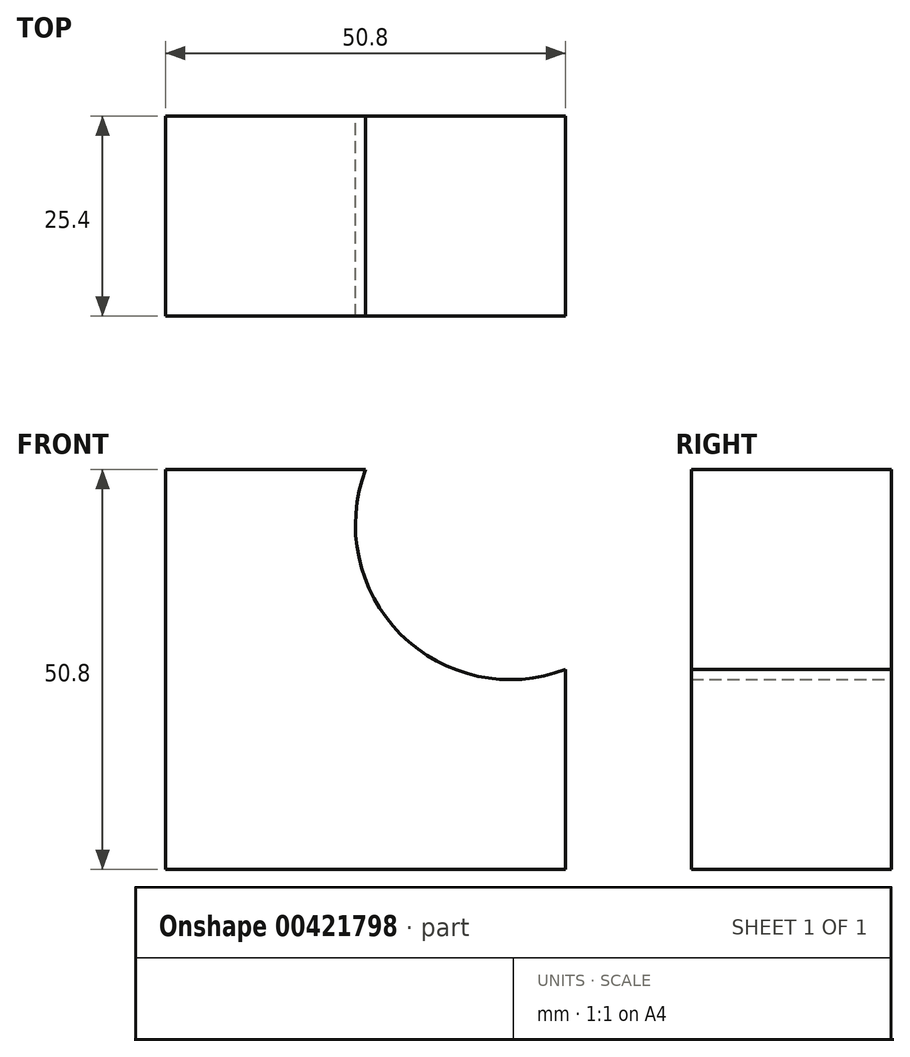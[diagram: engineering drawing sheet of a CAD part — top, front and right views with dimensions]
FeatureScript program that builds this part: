
annotation { "Feature Type Name" : "Feature", "Feature Type Description" : "" }
export const myFeature = defineFeature(function(context is Context, id is Id, definition is map)
    precondition{}
    {
        {
            var Q0;
            Q0=qCreatedBy(makeId("Front.planeOp"),FACE);
            var sketch = newSketch(context, id + "F0", { "sketchPlane" : qUnion([Q0])});
            skLineSegment(sketch, "E0", {"start": v(0, 0) * mm, "end": v(-50.8, 0) * mm});
            skLineSegment(sketch, "E1", {"start": v(-50.8, 0) * mm, "end": v(-50.8, 50.8) * mm});
            skLineSegment(sketch, "E2", {"start": v(-50.8, 50.8) * mm, "end": v(-25.4, 50.8) * mm});
            skLineSegment(sketch, "E3", {"start": v(0, 0) * mm, "end": v(0, 25.4) * mm});
            skArc(sketch, "E4", {"start": v(-25.4, 50.8) * mm, "mid": v(-20.93, 29.87) * mm, "end": v(0, 25.4) * mm});
            skSolve(sketch);
        }
        {
            var Q0;
            Q0 = qSketchRegion(id + "F0", true);
            extrude(context, id + "F1", {"entities" : qUnion([Q0]), "depth" : 25.4 * mm});
        }
    });
